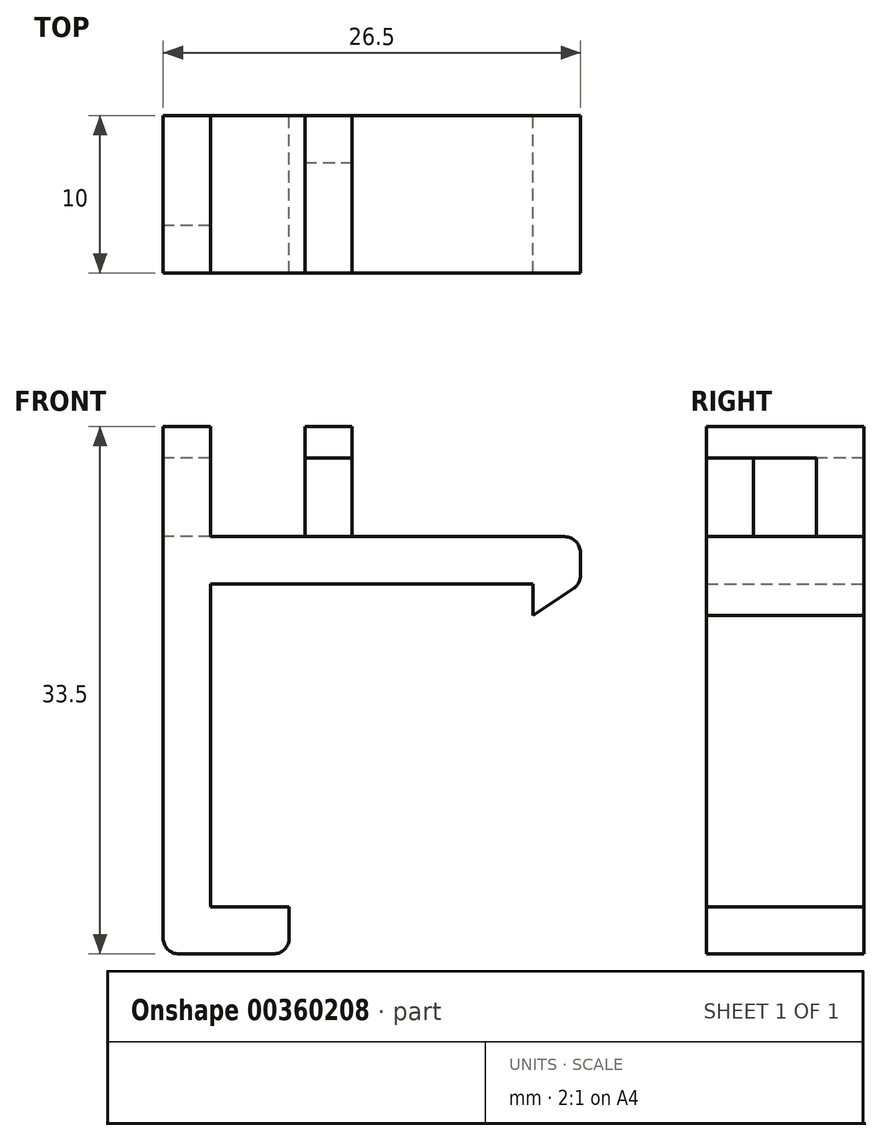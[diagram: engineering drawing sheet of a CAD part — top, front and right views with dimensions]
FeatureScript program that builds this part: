
annotation { "Feature Type Name" : "Feature", "Feature Type Description" : "" }
export const myFeature = defineFeature(function(context is Context, id is Id, definition is map)
    precondition{}
    {
        {
            var Q0;
            Q0=qCreatedBy(makeId("Front.planeOp"),FACE);
            var sketch = newSketch(context, id + "F0", { "sketchPlane" : qUnion([Q0])});
            skLineSegment(sketch, "E0", {"start": v(5, 0) * mm, "end": v(0, 0) * mm});
            skLineSegment(sketch, "E1", {"start": v(0, 0) * mm, "end": v(0, 20.5) * mm});
            skLineSegment(sketch, "E2", {"start": v(0, 20.5) * mm, "end": v(20.5, 20.5) * mm});
            skLineSegment(sketch, "E3", {"start": v(20.5, 20.5) * mm, "end": v(20.5, 18.5) * mm});
            skLineSegment(sketch, "E4", {"start": v(20.5, 18.5) * mm, "end": v(23.5, 20.5) * mm});
            skLineSegment(sketch, "E5", {"start": v(23.5, 20.5) * mm, "end": v(23.5, 23.5) * mm});
            skLineSegment(sketch, "E6", {"start": v(23.5, 23.5) * mm, "end": v(9, 23.5) * mm});
            skLineSegment(sketch, "E7", {"start": v(-3, 23.5) * mm, "end": v(-3, -3) * mm});
            skLineSegment(sketch, "E8", {"start": v(-3, -3) * mm, "end": v(5, -3) * mm});
            skLineSegment(sketch, "E9", {"start": v(5, -3) * mm, "end": v(5, 0) * mm});
            skLineSegment(sketch, "E10", {"start": v(-3, 23.5) * mm, "end": v(-3, 30.5) * mm});
            skLineSegment(sketch, "E11", {"start": v(-3, 30.5) * mm, "end": v(0, 30.5) * mm});
            skLineSegment(sketch, "E12", {"start": v(0, 30.5) * mm, "end": v(0, 23.5) * mm});
            skLineSegment(sketch, "E13.top", {"start": v(6, 30.5) * mm, "end": v(9, 30.5) * mm});
            skLineSegment(sketch, "E13.left", {"start": v(6, 23.5) * mm, "end": v(6, 30.5) * mm});
            skLineSegment(sketch, "E13.right", {"start": v(9, 23.5) * mm, "end": v(9, 30.5) * mm});
            skLineSegment(sketch, "E14.trimOffspring", {"start": v(6, 23.5) * mm, "end": v(0, 23.5) * mm});
            skSolve(sketch);
        }
        {
            var Q0;
            Q0 = qSketchRegion(id + "F0", true);
            extrude(context, id + "F1", {"entities" : qUnion([Q0]), "depth" : 10 * mm});
        }
        {
            var Q0;
            Q0=makeQuery(id+"F1.opExtrude","SWEPT_EDGE",EDGE,{"disambiguationData":[OSD([sQuery(id+"F0.wireOp",EDGE,"E5"),sQuery(id+"F0.wireOp",EDGE,"E6")])]});
            var Q1;
            Q1=makeQuery(id+"F1.opExtrude","SWEPT_EDGE",EDGE,{"disambiguationData":[OSD([sQuery(id+"F0.wireOp",EDGE,"E5"),sQuery(id+"F0.wireOp",EDGE,"E6")])]});
            var Q2;
            Q2=makeQuery(id+"F1.opExtrude","SWEPT_EDGE",EDGE,{"disambiguationData":[OSD([sQuery(id+"F0.wireOp",EDGE,"E7"),sQuery(id+"F0.wireOp",EDGE,"E8")])]});
            var Q3;
            Q3=makeQuery(id+"F1.opExtrude","SWEPT_EDGE",EDGE,{"disambiguationData":[OSD([sQuery(id+"F0.wireOp",EDGE,"E5"),sQuery(id+"F0.wireOp",EDGE,"E6")])]});
            var Q4;
            Q4=makeQuery(id+"F1.opExtrude","SWEPT_EDGE",EDGE,{"disambiguationData":[OSD([sQuery(id+"F0.wireOp",EDGE,"E5"),sQuery(id+"F0.wireOp",EDGE,"E6")])]});
            var Q5;
            Q5=makeQuery(id+"F1.opExtrude","SWEPT_EDGE",EDGE,{"disambiguationData":[OSD([sQuery(id+"F0.wireOp",EDGE,"E4"),sQuery(id+"F0.wireOp",EDGE,"E5")])]});
            var Q6;
            Q6=makeQuery(id+"F1.opExtrude","SWEPT_EDGE",EDGE,{"disambiguationData":[OSD([sQuery(id+"F0.wireOp",EDGE,"E8"),sQuery(id+"F0.wireOp",EDGE,"E9")])]});
            fillet(context, id + "F2", {"entities" : qUnion([Q0, Q1, Q2, Q3, Q4, Q5, Q6]), "radius" : 1 * mm, "tangentPropagation" : true, "allowEdgeOverflow" : false});
        }
        {
            var Q0;
            Q0=makeQuery(id+"F1.opExtrude","SWEPT_FACE",FACE,{"disambiguationData":[OSD([sQuery(id+"F0.wireOp",EDGE,"E7"),sQuery(id+"F0.wireOp",EDGE,"E10")])]});
            var sketch = newSketch(context, id + "F3", { "sketchPlane" : qUnion([Q0])});
            skLineSegment(sketch, "E15.bottom", {"start": v(0, 23.5) * mm, "end": v(7, 23.5) * mm});
            skLineSegment(sketch, "E15.top", {"start": v(0, 28.5) * mm, "end": v(7, 28.5) * mm});
            skLineSegment(sketch, "E15.left", {"start": v(0, 23.5) * mm, "end": v(0, 28.5) * mm});
            skLineSegment(sketch, "E15.right", {"start": v(7, 23.5) * mm, "end": v(7, 28.5) * mm});
            skSolve(sketch);
        }
        {
            var Q0;
            Q0 = qSketchRegion(id + "F3", true);
            extrude(context, id + "F4", {"entities" : qUnion([Q0]), "operationType" : NewBodyOperationType.REMOVE, "endBound" : BoundingType.UP_TO_NEXT, "oppositeDirection" : true, "depth" : 25 * mm});
        }
        {
            var Q0;
            Q0=makeQuery(id+"F1.opExtrude","SWEPT_FACE",FACE,{"disambiguationData":[OSD([sQuery(id+"F0.wireOp",EDGE,"E13.right")])]});
            var sketch = newSketch(context, id + "F5", { "sketchPlane" : qUnion([Q0])});
            skLineSegment(sketch, "E16.bottom", {"start": v(-10, 23.5) * mm, "end": v(-3, 23.5) * mm});
            skLineSegment(sketch, "E16.top", {"start": v(-10, 28.5) * mm, "end": v(-3, 28.5) * mm});
            skLineSegment(sketch, "E16.left", {"start": v(-10, 23.5) * mm, "end": v(-10, 28.5) * mm});
            skLineSegment(sketch, "E16.right", {"start": v(-3, 23.5) * mm, "end": v(-3, 28.5) * mm});
            skSolve(sketch);
        }
        {
            var Q0;
            Q0 = qSketchRegion(id + "F5", true);
            extrude(context, id + "F6", {"entities" : qUnion([Q0]), "operationType" : NewBodyOperationType.REMOVE, "endBound" : BoundingType.UP_TO_NEXT, "oppositeDirection" : true, "depth" : 25 * mm});
        }
    });
